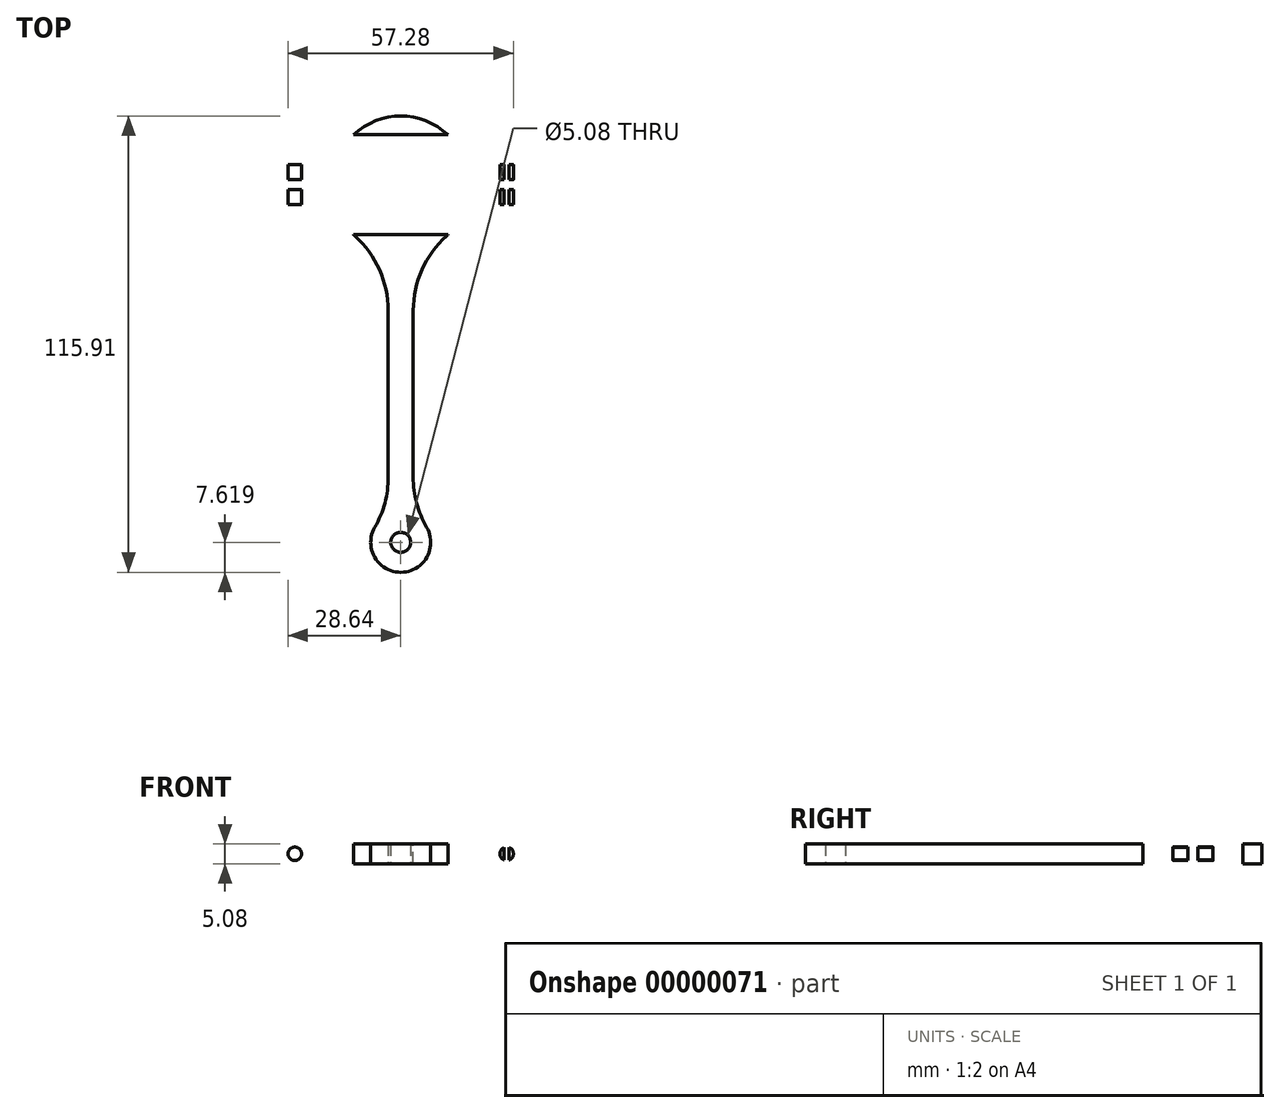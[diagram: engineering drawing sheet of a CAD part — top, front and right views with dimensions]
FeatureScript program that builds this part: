
annotation { "Feature Type Name" : "Feature", "Feature Type Description" : "" }
export const myFeature = defineFeature(function(context is Context, id is Id, definition is map)
    precondition{}
    {
        {
            var Q0;
            Q0=qCreatedBy(makeId("Top.planeOp"),FACE);
            var sketch = newSketch(context, id + "F0", { "sketchPlane" : qUnion([Q0])});
            skCircle(sketch, "E0", {"center": v(0, 0) * mm, "radius": 11.11 * mm});
            skCircle(sketch, "E1", {"center": v(0, 0) * mm, "radius": 17.46 * mm});
            skLineSegment(sketch, "E2.rect.top", {"start": v(-3.17, -93.37) * mm, "end": v(3.18, -93.37) * mm});
            skLineSegment(sketch, "E2.rect.left", {"start": v(-3.17, -17.17) * mm, "end": v(-3.17, -93.37) * mm});
            skLineSegment(sketch, "E2.rect.right", {"start": v(3.18, -17.17) * mm, "end": v(3.18, -93.37) * mm});
            skPoint(sketch, "E2.rect.middle", {"position": v(0, -55.27) * mm});
            skLineSegment(sketch, "E3", {"start": v(0, 0) * mm, "end": v(11.11, 0) * mm, "construction": true});
            skLineSegment(sketch, "E4", {"start": v(0, 0) * mm, "end": v(0, 11.11) * mm, "construction": true});
            skLineSegment(sketch, "E5", {"start": v(-11.04, 1.27) * mm, "end": v(-35.76, 1.27) * mm});
            skLineSegment(sketch, "E6", {"start": v(-35.76, 1.27) * mm, "end": v(-35.76, 5.08) * mm});
            skLineSegment(sketch, "E7", {"start": v(-35.76, 5.08) * mm, "end": v(-16.7, 5.08) * mm});
            skLineSegment(sketch, "E8.0.MirrorCS", {"start": v(35.76, 5.08) * mm, "end": v(16.7, 5.08) * mm});
            skLineSegment(sketch, "E8.1.MirrorCS", {"start": v(35.76, 1.27) * mm, "end": v(35.76, 5.08) * mm});
            skLineSegment(sketch, "E8.2.MirrorCS", {"start": v(11.04, 1.27) * mm, "end": v(35.76, 1.27) * mm});
            skLineSegment(sketch, "E9.0.MirrorCS", {"start": v(-35.76, -5.08) * mm, "end": v(-16.7, -5.08) * mm});
            skLineSegment(sketch, "E9.1.MirrorCS", {"start": v(-35.76, -1.27) * mm, "end": v(-35.76, -5.08) * mm});
            skLineSegment(sketch, "E9.2.MirrorCS", {"start": v(-11.04, -1.27) * mm, "end": v(-35.76, -1.27) * mm});
            skLineSegment(sketch, "E9.3.MirrorCS", {"start": v(35.76, -1.27) * mm, "end": v(35.76, -5.08) * mm});
            skLineSegment(sketch, "E9.4.MirrorCS", {"start": v(35.76, -5.08) * mm, "end": v(16.7, -5.08) * mm});
            skLineSegment(sketch, "E9.5.MirrorCS", {"start": v(11.04, -1.27) * mm, "end": v(35.76, -1.27) * mm});
            skSolve(sketch);
        }
        {
            var Q0;
            {var subQ3=sQuery(id+"F0.wireOp",EDGE,"E0");var subQ6=sQuery(id+"F0.wireOp",EDGE,"E9.2.MirrorCS");var subQ8=makeQuery(id+"F0.imprint","INTERSECT",VERTEX,{"derivedFrom":[subQ3,subQ6]});Q0=makeQuery(id+"F0.imprint","IMPRINT",FACE,{"disambiguationData":[TD([[makeQuery(id+"F0.imprint","IMPRINT",EDGE,{"disambiguationData":[TD([[subQ8,-1.0]])],"derivedFrom":subQ3}),-1.0]])]});}
            var Q1;
            Q1=makeQuery(id+"F0.imprint","IMPRINT",FACE,{"disambiguationData":[TD([[makeQuery(id+"F0.imprint","IMPRINT",EDGE,{"derivedFrom":sQuery(id+"F0.wireOp",EDGE,"E2.rect.top")}),1.0]])]});
            var Q2;
            {var subQ4=sQuery(id+"F0.wireOp",EDGE,"E9.0.MirrorCS");Q2=makeQuery(id+"F0.imprint","IMPRINT",FACE,{"disambiguationData":[TD([[makeQuery(id+"F0.imprint","IMPRINT",EDGE,{"derivedFrom":subQ4}),1.0]])]});}
            var Q3;
            {var subQ1=sQuery(id+"F0.wireOp",EDGE,"E6");Q3=makeQuery(id+"F0.imprint","IMPRINT",FACE,{"disambiguationData":[TD([[makeQuery(id+"F0.imprint","IMPRINT",EDGE,{"derivedFrom":subQ1}),-1.0]])]});}
            var Q4;
            {var subQ3=sQuery(id+"F0.wireOp",EDGE,"E0");var subQ5=sQuery(id+"F0.wireOp",EDGE,"E5");var subQ7=makeQuery(id+"F0.imprint","INTERSECT",VERTEX,{"derivedFrom":[subQ3,subQ5]});Q4=makeQuery(id+"F0.imprint","IMPRINT",FACE,{"disambiguationData":[TD([[makeQuery(id+"F0.imprint","IMPRINT",EDGE,{"disambiguationData":[TD([[subQ7,1.0]])],"derivedFrom":subQ3}),-1.0]])]});}
            var Q5;
            {var subQ4=sQuery(id+"F0.wireOp",EDGE,"E8.0.MirrorCS");Q5=makeQuery(id+"F0.imprint","IMPRINT",FACE,{"disambiguationData":[TD([[makeQuery(id+"F0.imprint","IMPRINT",EDGE,{"derivedFrom":subQ4}),1.0]])]});}
            var Q6;
            {var subQ3=sQuery(id+"F0.wireOp",EDGE,"E9.3.MirrorCS");Q6=makeQuery(id+"F0.imprint","IMPRINT",FACE,{"disambiguationData":[TD([[makeQuery(id+"F0.imprint","IMPRINT",EDGE,{"derivedFrom":subQ3}),-1.0]])]});}
            extrude(context, id + "F1", {"entities" : qUnion([Q0, Q1, Q2, Q3, Q4, Q5, Q6]), "depth" : 12.7 * mm, "symmetric" : true});
        }
        {
            var Q0;
            Q0=makeQuery(id+"F1.opExtrude","SWEPT_EDGE",EDGE,{"disambiguationData":[OSD([sQuery(id+"F0.wireOp",EDGE,"E1"),sQuery(id+"F0.wireOp",EDGE,"E2.rect.left")])]});
            var Q1;
            Q1=makeQuery(id+"F1.opExtrude","SWEPT_EDGE",EDGE,{"disambiguationData":[OSD([sQuery(id+"F0.wireOp",EDGE,"E1"),sQuery(id+"F0.wireOp",EDGE,"E2.rect.right")])]});
            fillet(context, id + "F2", {"entities" : qUnion([Q0, Q1]), "radius" : 25.4 * mm, "tangentPropagation" : true, "allowEdgeOverflow" : false});
        }
        {
            var Q0;
            Q0=makeQuery(id+"F1.opExtrude","SWEPT_EDGE",EDGE,{"disambiguationData":[OSD([sQuery(id+"F0.wireOp",EDGE,"E1"),sQuery(id+"F0.wireOp",EDGE,"E9.0.MirrorCS")])]});
            var Q1;
            Q1=makeQuery(id+"F1.opExtrude","SWEPT_EDGE",EDGE,{"disambiguationData":[OSD([sQuery(id+"F0.wireOp",EDGE,"E1"),sQuery(id+"F0.wireOp",EDGE,"E7")])]});
            var Q2;
            Q2=makeQuery(id+"F1.opExtrude","SWEPT_EDGE",EDGE,{"disambiguationData":[OSD([sQuery(id+"F0.wireOp",EDGE,"E1"),sQuery(id+"F0.wireOp",EDGE,"E8.0.MirrorCS")])]});
            var Q3;
            Q3=makeQuery(id+"F1.opExtrude","SWEPT_EDGE",EDGE,{"disambiguationData":[OSD([sQuery(id+"F0.wireOp",EDGE,"E1"),sQuery(id+"F0.wireOp",EDGE,"E9.4.MirrorCS")])]});
            var Q4;
            Q4=makeQuery(id+"F1.opExtrude","SWEPT_EDGE",EDGE,{"disambiguationData":[OSD([sQuery(id+"F0.wireOp",EDGE,"E0"),sQuery(id+"F0.wireOp",EDGE,"E5")])]});
            var Q5;
            Q5=makeQuery(id+"F1.opExtrude","SWEPT_EDGE",EDGE,{"disambiguationData":[OSD([sQuery(id+"F0.wireOp",EDGE,"E0"),sQuery(id+"F0.wireOp",EDGE,"E9.2.MirrorCS")])]});
            var Q6;
            Q6=makeQuery(id+"F1.opExtrude","SWEPT_EDGE",EDGE,{"disambiguationData":[OSD([sQuery(id+"F0.wireOp",EDGE,"E0"),sQuery(id+"F0.wireOp",EDGE,"E8.2.MirrorCS")])]});
            var Q7;
            Q7=makeQuery(id+"F1.opExtrude","SWEPT_EDGE",EDGE,{"disambiguationData":[OSD([sQuery(id+"F0.wireOp",EDGE,"E0"),sQuery(id+"F0.wireOp",EDGE,"E9.5.MirrorCS")])]});
            fillet(context, id + "F3", {"entities" : qUnion([Q0, Q1, Q2, Q3, Q4, Q5, Q6, Q7]), "radius" : 5.08 * mm, "tangentPropagation" : true, "allowEdgeOverflow" : false});
        }
        {
            var Q0;
            Q0=qCreatedBy(makeId("Front.planeOp"),FACE);
            var sketch = newSketch(context, id + "F4", { "sketchPlane" : qUnion([Q0])});
            skLineSegment(sketch, "E10.rect.bottom", {"start": v(35.76, -6.35) * mm, "end": v(-35.76, -6.35) * mm});
            skLineSegment(sketch, "E10.rect.top", {"start": v(35.76, 6.35) * mm, "end": v(-35.76, 6.35) * mm});
            skLineSegment(sketch, "E10.rect.left", {"start": v(35.76, -6.35) * mm, "end": v(35.76, 6.35) * mm});
            skLineSegment(sketch, "E10.rect.right", {"start": v(-35.76, -6.35) * mm, "end": v(-35.76, 6.35) * mm});
            skPoint(sketch, "E10.rect.middle", {"position": v(0, 0) * mm});
            skArc(sketch, "E11", {"start": v(23.26, -4.14) * mm, "mid": v(32.45, 0) * mm, "end": v(23.26, 4.14) * mm});
            skCircle(sketch, "E12", {"center": v(26.92, 0) * mm, "radius": 1.71 * mm});
            skLineSegment(sketch, "E13", {"start": v(0, 0) * mm, "end": v(0, 6.35) * mm, "construction": true});
            skLineSegment(sketch, "E14", {"start": v(19.05, -2.54) * mm, "end": v(0, -2.54) * mm});
            skLineSegment(sketch, "E15", {"start": v(0, 0) * mm, "end": v(35.76, 0) * mm, "construction": true});
            skLineSegment(sketch, "E16.0.MirrorCS", {"start": v(19.05, 2.54) * mm, "end": v(0, 2.54) * mm});
            skPoint(sketch, "E17.visualSharp", {"position": v(22.02, -2.54) * mm});
            skArc(sketch, "E17.filletArc", {"start": v(23.26, -4.14) * mm, "mid": v(21.3, -2.95) * mm, "end": v(19.05, -2.54) * mm});
            skPoint(sketch, "E18.visualSharp", {"position": v(22.02, 2.54) * mm});
            skArc(sketch, "E18.filletArc", {"start": v(19.05, 2.54) * mm, "mid": v(21.3, 2.95) * mm, "end": v(23.26, 4.14) * mm});
            skLineSegment(sketch, "E19.0.MirrorCS", {"start": v(-19.05, 2.54) * mm, "end": v(0, 2.54) * mm});
            skLineSegment(sketch, "E19.1.MirrorCS", {"start": v(-19.05, -2.54) * mm, "end": v(0, -2.54) * mm});
            skArc(sketch, "E19.2.MirrorCS", {"start": v(-23.26, -4.14) * mm, "mid": v(-21.3, -2.95) * mm, "end": v(-19.05, -2.54) * mm});
            skArc(sketch, "E19.3.MirrorCS", {"start": v(-19.05, 2.54) * mm, "mid": v(-21.3, 2.95) * mm, "end": v(-23.26, 4.14) * mm});
            skCircle(sketch, "E19.4.MirrorC", {"center": v(-26.92, 0) * mm, "radius": 1.71 * mm});
            skArc(sketch, "E19.5.MirrorCS", {"start": v(-23.26, -4.14) * mm, "mid": v(-32.45, 0) * mm, "end": v(-23.26, 4.14) * mm});
            skLineSegment(sketch, "E20.rect.bottom", {"start": v(-27.56, -2.54) * mm, "end": v(-26.29, -2.54) * mm});
            skLineSegment(sketch, "E20.rect.top", {"start": v(-27.56, 2.54) * mm, "end": v(-26.29, 2.54) * mm});
            skLineSegment(sketch, "E20.rect.left", {"start": v(-27.56, -2.54) * mm, "end": v(-27.56, 2.54) * mm});
            skLineSegment(sketch, "E20.rect.right", {"start": v(-26.29, -2.54) * mm, "end": v(-26.29, 2.54) * mm});
            skLineSegment(sketch, "E21.rect.bottom", {"start": v(26.29, -2.54) * mm, "end": v(27.56, -2.54) * mm});
            skLineSegment(sketch, "E21.rect.top", {"start": v(26.29, 2.54) * mm, "end": v(27.56, 2.54) * mm});
            skLineSegment(sketch, "E21.rect.left", {"start": v(26.29, -2.54) * mm, "end": v(26.29, 2.54) * mm});
            skLineSegment(sketch, "E21.rect.right", {"start": v(27.56, -2.54) * mm, "end": v(27.56, 2.54) * mm});
            skSolve(sketch);
        }
        {
            var Q0;
            Q0 = qSketchRegion(id + "F4", true);
            extrude(context, id + "F5", {"entities" : qUnion([Q0]), "operationType" : NewBodyOperationType.REMOVE, "oppositeDirection" : true, "depth" : 254 * mm, "symmetric" : true});
        }
        {
            var Q0;
            Q0=makeQuery(id+"F4.imprint","IMPRINT",FACE,{"disambiguationData":[TD([[makeQuery(id+"F4.imprint","IMPRINT",EDGE,{"derivedFrom":sQuery(id+"F4.wireOp",EDGE,"E12")}),1.0]])]});
            var Q1;
            Q1=makeQuery(id+"F4.imprint","IMPRINT",FACE,{"disambiguationData":[TD([[makeQuery(id+"F4.imprint","IMPRINT",EDGE,{"derivedFrom":sQuery(id+"F4.wireOp",EDGE,"E19.4.MirrorC")}),-1.0]])]});
            var Q2;
            {var subQ3=sQuery(id+"F4.wireOp",EDGE,"E20.rect.top");Q2=makeQuery(id+"F4.imprint","IMPRINT",FACE,{"disambiguationData":[TD([[makeQuery(id+"F4.imprint","IMPRINT",EDGE,{"derivedFrom":subQ3}),-1.0]])]});}
            var Q3;
            {var subQ3=sQuery(id+"F4.wireOp",EDGE,"E20.rect.bottom");Q3=makeQuery(id+"F4.imprint","IMPRINT",FACE,{"disambiguationData":[TD([[makeQuery(id+"F4.imprint","IMPRINT",EDGE,{"derivedFrom":subQ3}),1.0]])]});}
            var Q4;
            {var subQ3=sQuery(id+"F4.wireOp",EDGE,"E21.rect.bottom");Q4=makeQuery(id+"F4.imprint","IMPRINT",FACE,{"disambiguationData":[TD([[makeQuery(id+"F4.imprint","IMPRINT",EDGE,{"derivedFrom":subQ3}),1.0]])]});}
            var Q5;
            {var subQ0=sQuery(id+"F4.wireOp",EDGE,"E21.rect.left");var subQ1=sQuery(id+"F4.wireOp",EDGE,"E12");var subQ3=makeQuery(id+"F4.imprint","INTERSECT",VERTEX,{"disambiguationData":[OD(0.0)],"derivedFrom":[subQ1,subQ0]});Q5=makeQuery(id+"F4.imprint","IMPRINT",FACE,{"disambiguationData":[TD([[makeQuery(id+"F4.imprint","IMPRINT",EDGE,{"disambiguationData":[TD([[subQ3,-1.0]])],"derivedFrom":subQ1}),1.0]])]});}
            var Q6;
            {var subQ0=sQuery(id+"F4.wireOp",EDGE,"E21.rect.right");var subQ1=sQuery(id+"F4.wireOp",EDGE,"E12");var subQ3=makeQuery(id+"F4.imprint","INTERSECT",VERTEX,{"disambiguationData":[OD(0.0)],"derivedFrom":[subQ1,subQ0]});Q6=makeQuery(id+"F4.imprint","IMPRINT",FACE,{"disambiguationData":[TD([[makeQuery(id+"F4.imprint","IMPRINT",EDGE,{"disambiguationData":[TD([[subQ3,1.0]])],"derivedFrom":subQ1}),1.0]])]});}
            var Q7;
            {var subQ3=sQuery(id+"F4.wireOp",EDGE,"E21.rect.top");Q7=makeQuery(id+"F4.imprint","IMPRINT",FACE,{"disambiguationData":[TD([[makeQuery(id+"F4.imprint","IMPRINT",EDGE,{"derivedFrom":subQ3}),-1.0]])]});}
            var Q8;
            {var subQ0=sQuery(id+"F4.wireOp",EDGE,"E20.rect.right");var subQ1=sQuery(id+"F4.wireOp",EDGE,"E19.4.MirrorC");var subQ3=makeQuery(id+"F4.imprint","INTERSECT",VERTEX,{"disambiguationData":[OD(0.0)],"derivedFrom":[subQ1,subQ0]});Q8=makeQuery(id+"F4.imprint","IMPRINT",FACE,{"disambiguationData":[TD([[makeQuery(id+"F4.imprint","IMPRINT",EDGE,{"disambiguationData":[TD([[subQ3,-1.0]])],"derivedFrom":subQ1}),-1.0]])]});}
            var Q9;
            {var subQ0=sQuery(id+"F4.wireOp",EDGE,"E20.rect.left");var subQ1=sQuery(id+"F4.wireOp",EDGE,"E19.4.MirrorC");var subQ3=makeQuery(id+"F4.imprint","INTERSECT",VERTEX,{"disambiguationData":[OD(0.0)],"derivedFrom":[subQ1,subQ0]});Q9=makeQuery(id+"F4.imprint","IMPRINT",FACE,{"disambiguationData":[TD([[makeQuery(id+"F4.imprint","IMPRINT",EDGE,{"disambiguationData":[TD([[subQ3,1.0]])],"derivedFrom":subQ1}),-1.0]])]});}
            extrude(context, id + "F6", {"entities" : qUnion([Q0, Q1, Q2, Q3, Q4, Q5, Q6, Q7, Q8, Q9]), "operationType" : NewBodyOperationType.REMOVE, "oppositeDirection" : true, "depth" : 25.4 * mm, "symmetric" : true});
        }
        {
            var Q0;
            Q0=makeQuery(id+"F5.boolean.opBoolean","COPY",FACE,{"disambiguationData":[OD(1.0)],"derivedFrom":makeQuery(id+"F5.opExtrude","SWEPT_FACE",FACE,{"disambiguationData":[OSD([sQuery(id+"F4.wireOp",EDGE,"E14"),sQuery(id+"F4.wireOp",EDGE,"E19.1.MirrorCS")])]})});
            var sketch = newSketch(context, id + "F7", { "sketchPlane" : qUnion([Q0])});
            skCircle(sketch, "E22", {"center": v(0, 90.83) * mm, "radius": 2.54 * mm});
            skCircle(sketch, "E23", {"center": v(0, 90.83) * mm, "radius": 7.62 * mm});
            skSolve(sketch);
        }
        {
            var Q0;
            Q0 = qSketchRegion(id + "F7", true);
            var Q1;
            Q1=makeQuery(id+"F5.boolean.opBoolean","COPY",FACE,{"disambiguationData":[OD(1.0)],"derivedFrom":makeQuery(id+"F5.opExtrude","SWEPT_FACE",FACE,{"disambiguationData":[OSD([sQuery(id+"F4.wireOp",EDGE,"E16.0.MirrorCS"),sQuery(id+"F4.wireOp",EDGE,"E19.0.MirrorCS")])]})});
            extrude(context, id + "F8", {"entities" : qUnion([Q0]), "operationType" : NewBodyOperationType.ADD, "endBound" : BoundingType.UP_TO_SURFACE, "oppositeDirection" : true, "endBoundEntityFace" : qUnion([Q1]), "depth" : 25.4 * mm});
        }
        {
            var Q0;
            Q0=makeQuery(id+"F7.imprint","IMPRINT",FACE,{"disambiguationData":[TD([[makeQuery(id+"F7.imprint","IMPRINT",EDGE,{"derivedFrom":sQuery(id+"F7.wireOp",EDGE,"E22")}),1.0]])]});
            extrude(context, id + "F9", {"entities" : qUnion([Q0]), "operationType" : NewBodyOperationType.REMOVE, "endBound" : BoundingType.UP_TO_NEXT, "oppositeDirection" : true, "depth" : 25.4 * mm});
        }
        {
            var Q0;
            Q0=makeQuery(id+"F8.boolean.opBoolean","INTERSECT",EDGE,{"derivedFrom":[makeQuery(id+"F1.opExtrude","SWEPT_FACE",FACE,{"disambiguationData":[OSD([sQuery(id+"F0.wireOp",EDGE,"E2.rect.right")])]}),makeQuery(id+"F8.opExtrude","SWEPT_FACE",FACE,{"disambiguationData":[OSD([sQuery(id+"F7.wireOp",EDGE,"E23")])]})]});
            var Q1;
            Q1=makeQuery(id+"F8.boolean.opBoolean","INTERSECT",EDGE,{"derivedFrom":[makeQuery(id+"F1.opExtrude","SWEPT_FACE",FACE,{"disambiguationData":[OSD([sQuery(id+"F0.wireOp",EDGE,"E2.rect.left")])]}),makeQuery(id+"F8.opExtrude","SWEPT_FACE",FACE,{"disambiguationData":[OSD([sQuery(id+"F7.wireOp",EDGE,"E23")])]})]});
            fillet(context, id + "F10", {"entities" : qUnion([Q0, Q1]), "radius" : 25.4 * mm, "tangentPropagation" : true, "allowEdgeOverflow" : false});
        }
    });
